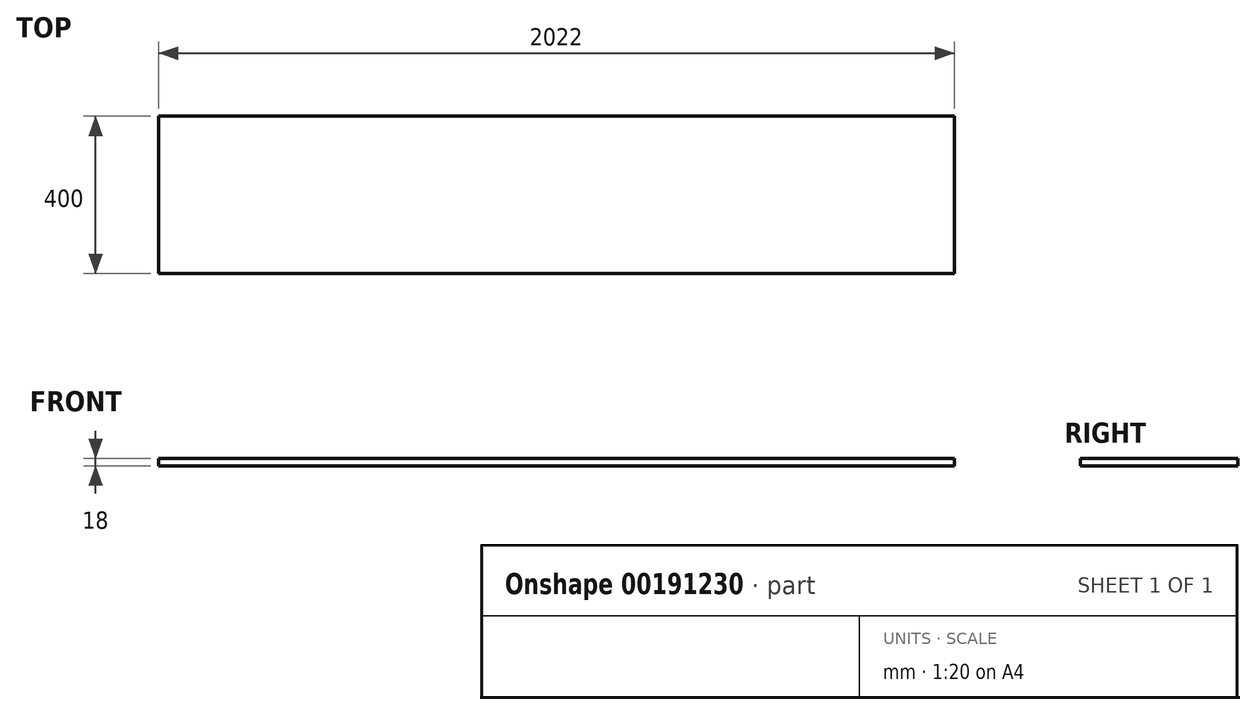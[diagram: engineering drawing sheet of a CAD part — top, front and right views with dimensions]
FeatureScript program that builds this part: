
annotation { "Feature Type Name" : "Feature", "Feature Type Description" : "" }
export const myFeature = defineFeature(function(context is Context, id is Id, definition is map)
    precondition{}
    {
        {
            var Q0;
            Q0=qCreatedBy(makeId("Top.planeOp"),FACE);
            var sketch = newSketch(context, id + "F0", { "sketchPlane" : qUnion([Q0])});
            skLineSegment(sketch, "E0.bottom", {"start": v(0, 0) * mm, "end": v(2022, 0) * mm});
            skLineSegment(sketch, "E0.top", {"start": v(0, 400) * mm, "end": v(2022, 400) * mm});
            skLineSegment(sketch, "E0.left", {"start": v(0, 0) * mm, "end": v(0, 400) * mm});
            skLineSegment(sketch, "E0.right", {"start": v(2022, 0) * mm, "end": v(2022, 400) * mm});
            skSolve(sketch);
        }
        {
            var Q0;
            Q0 = qSketchRegion(id + "F0", true);
            extrude(context, id + "F1", {"entities" : qUnion([Q0]), "depth" : 18 * mm});
        }
    });
